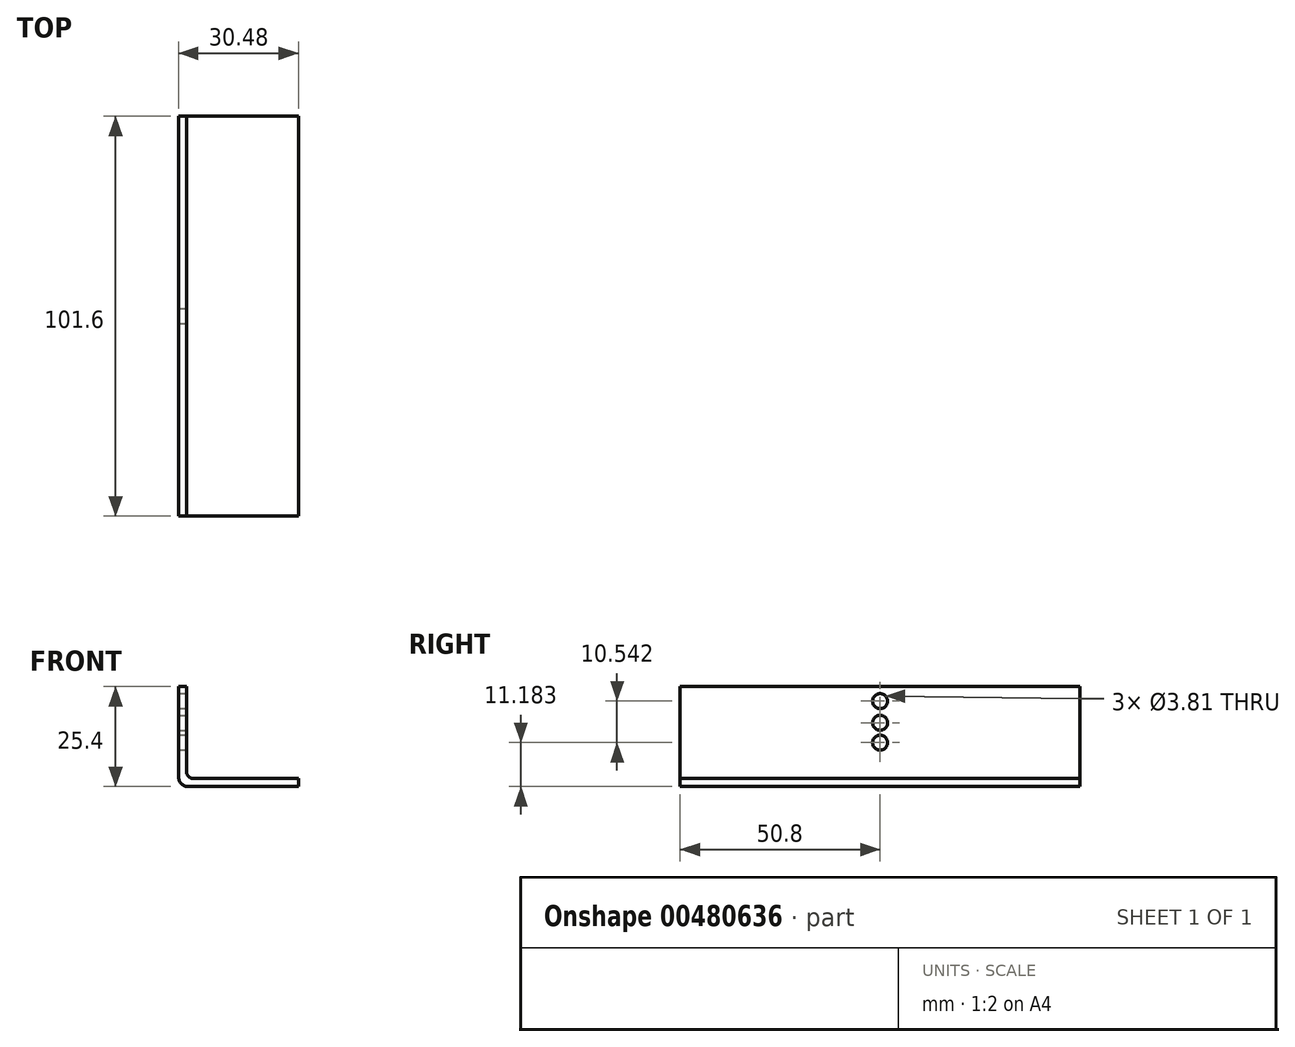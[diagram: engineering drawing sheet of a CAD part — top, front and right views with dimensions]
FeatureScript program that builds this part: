
annotation { "Feature Type Name" : "Feature", "Feature Type Description" : "" }
export const myFeature = defineFeature(function(context is Context, id is Id, definition is map)
    precondition{}
    {
        {
            var Q0;
            Q0=qCreatedBy(makeId("Front.planeOp"),FACE);
            var sketch = newSketch(context, id + "F0", { "sketchPlane" : qUnion([Q0])});
            skLineSegment(sketch, "E0", {"start": v(-24.89, 12.97) * mm, "end": v(-55.37, 12.97) * mm});
            skLineSegment(sketch, "E1", {"start": v(-55.37, 12.97) * mm, "end": v(-55.37, 38.37) * mm});
            skLineSegment(sketch, "E2.0", {"start": v(-53.34, 12.97) * mm, "end": v(-53.34, 38.37) * mm});
            skLineSegment(sketch, "E3.0", {"start": v(-24.89, 15) * mm, "end": v(-55.37, 15) * mm});
            skLineSegment(sketch, "E4", {"start": v(-24.89, 12.97) * mm, "end": v(-24.89, 15) * mm});
            skLineSegment(sketch, "E5", {"start": v(-53.34, 38.37) * mm, "end": v(-55.37, 38.37) * mm});
            skSolve(sketch);
        }
        {
            var Q0;
            Q0=qSketchRegion(id+"F0",true);
            extrude(context, id + "F1", {"entities" : qUnion([Q0]), "depth" : 101.6 * mm, "symmetric" : true});
        }
        {
            var Q0;
            Q0=makeQuery(id+"F1.opExtrude","SWEPT_EDGE",EDGE,{"disambiguationData":[OSD([sQuery(id+"F0.wireOp",EDGE,"E0"),sQuery(id+"F0.wireOp",EDGE,"E1")])]});
            fillet(context, id + "F2", {"entities" : qUnion([Q0]), "radius" : 2.54 * mm, "tangentPropagation" : true, "allowEdgeOverflow" : false});
        }
        {
            var Q0;
            Q0=makeQuery(id+"F1.opExtrude","SWEPT_EDGE",EDGE,{"disambiguationData":[OSD([sQuery(id+"F0.wireOp",EDGE,"E2.0"),sQuery(id+"F0.wireOp",EDGE,"E3.0")])]});
            fillet(context, id + "F3", {"entities" : qUnion([Q0]), "radius" : 1.78 * mm, "tangentPropagation" : true, "allowEdgeOverflow" : false});
        }
        {
            var Q0;
            Q0=qCreatedBy(makeId("Right.planeOp"),FACE);
            var sketch = newSketch(context, id + "F4", { "sketchPlane" : qUnion([Q0])});
            skCircle(sketch, "E6", {"center": v(0, 34.7) * mm, "radius": 1.82 * mm});
            skCircle(sketch, "E7", {"center": v(0, 29.19) * mm, "radius": 1.82 * mm});
            skCircle(sketch, "E8", {"center": v(0, 24.15) * mm, "radius": 2.15 * mm});
            skSolve(sketch);
        }
        {
            var Q0;
            Q0=sQuery(id+"F4.wireOp",VERTEX,"E6.center");
            var Q1;
            Q1=sQuery(id+"F4.wireOp",VERTEX,"E7.center");
            var Q2;
            Q2=sQuery(id+"F4.wireOp",VERTEX,"E8.center");
            var Q3;
            Q3=makeQuery(id+"F1.opExtrude","SWEPT_BODY",BODY,{"disambiguationData":[OSD([sQuery(id+"F0.wireOp",EDGE,"E0"),sQuery(id+"F0.wireOp",EDGE,"E1"),sQuery(id+"F0.wireOp",EDGE,"E2.0"),sQuery(id+"F0.wireOp",EDGE,"E3.0"),sQuery(id+"F0.wireOp",EDGE,"E4"),sQuery(id+"F0.wireOp",EDGE,"E5")])]});
            hole(context, id + "F5", {"style" : HoleStyle.SIMPLE, "endStyle" : HoleEndStyle.THROUGH, "holeDiameter" : 3.8 * mm, "isTappedThrough" : true, "tappedDepth" : 12.7 * mm, "tapClearance" : 3, "locations" : qUnion([Q0, Q1, Q2]), "scope" : qUnion([Q3])});
        }
    });
